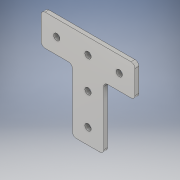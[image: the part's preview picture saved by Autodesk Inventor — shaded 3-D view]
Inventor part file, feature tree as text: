
AUTODESK INVENTOR PART (.ipt)
format: ipt  version: 2018 (Build 220112000, 112)  size: 145,920 bytes
history: native  units: in
note: dims shown in document units (in); Inventor stores cm internally (conversion verified against a paired STEP export)
features: extrude x2, sketch x2, fillet x1
ambient origin geometry x8: Origin, YZ Plane, XZ Plane, XY Plane, X Axis, Y Axis, Z Axis, Center Point
bodies: Solid1 (feature_tree)
feature tree (5):
  extrude  "Extrusion1"  Depth=3.0in
  extrude  "Extrusion2"  Depth=1.0in
  fillet  "Fillet1"  Radius=1.0in
  sketch  "Sketch1"  dims[d0=1.0in d1=3.0in]
  sketch  "Sketch2"  dims[d2=1.0in d3=1.0in d4=1.0in d5=1.0in d6=0.125in d7=0.0in d8=0.5in d9=1.0in d10=1.0in d11=1.0in d12=1.0in d13=0.2031in d14=0.125in d15=0.0in d16=0.125in]
